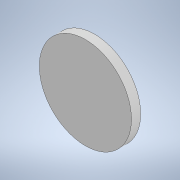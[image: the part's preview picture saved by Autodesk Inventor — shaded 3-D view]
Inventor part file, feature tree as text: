
AUTODESK INVENTOR PART (.ipt)
format: ipt  version: 2021 (Build 250183000, 183)  size: 92,160 bytes
history: native  units: mm
features: extrude x1, sketch x1
ambient origin geometry x8: Origin, YZ Plane, XZ Plane, XY Plane, X Axis, Y Axis, Z Axis, Center Point
bodies: Solid1 (feature_tree)
feature tree (2):
  extrude  "Extrusion1"  Depth=10.0mm
  sketch  "Sketch1"  dims[d0=10.0mm d1=0.0mm d2=100.0mm]
